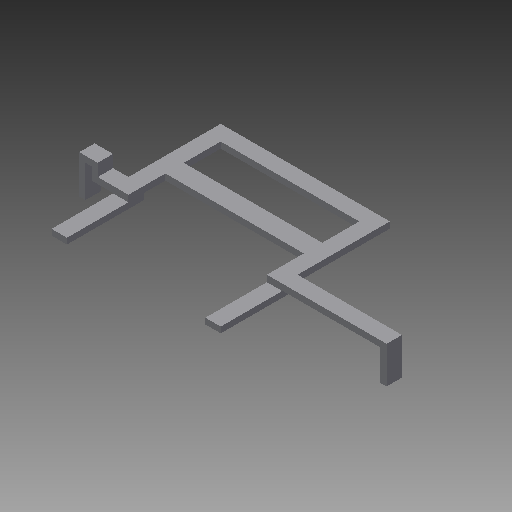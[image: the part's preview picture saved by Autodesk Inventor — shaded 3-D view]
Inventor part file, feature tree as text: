
AUTODESK INVENTOR PART (.ipt)
format: ipt  version: 2018.3 (Build 223284000, 284)  size: 192,512 bytes
history: native  units: mm
features: extrude x12, sketch x12
ambient origin geometry x8: Origin, YZ Plane, XZ Plane, XY Plane, X Axis, Y Axis, Z Axis, Center Point
bodies: Solid1 (feature_tree)
feature tree (24):
  extrude  "Extrusion1"  Depth=12.5mm
  extrude  "Extrusion2"  Depth=2.0mm
  extrude  "Extrusion3"  Depth=4.0mm
  extrude  "Extrusion4"  Depth=2.0mm
  extrude  "Extrusion5"  Depth=30.0mm TaperAngle=0.0deg
  extrude  "Extrusion6"  Depth=50.0mm TaperAngle=0.0deg
  extrude  "Extrusion7"  Depth=30.0mm TaperAngle=0.0deg
  extrude  "Extrusion8"  Depth=4.0mm TaperAngle=0.0deg
  extrude  "Extrusion9"  Depth=10.0mm TaperAngle=0.0deg
  extrude  "Extrusion10"  Depth=1.9mm
  extrude  "Extrusion11"  Depth=1.9mm
  extrude  "Extrusion12"  Depth=6.0mm
  sketch  "Sketch1"  dims[d0=2.0mm d1=12.5mm]
  sketch  "Sketch2"  dims[d2=4.0mm d3=2.0mm]
  sketch  "Sketch3"  dims[d4=2.0mm d5=4.0mm]
  sketch  "Sketch4"  dims[d6=5.0mm d7=0.0mm d8=2.0mm]
  sketch  "Sketch5"  dims[d9=10.0mm d10=0.0mm d11=30.0mm d12=0.0mm]
  sketch  "Sketch6"  dims[d13=5.0mm d14=50.0mm d15=0.0mm]
  sketch  "Sketch7"  dims[d16=5.0mm d17=30.0mm d18=0.0mm]
  sketch  "Sketch8"  dims[d19=29.93mm d20=0.0mm d21=4.0mm d22=0.0mm]
  sketch  "Sketch9"  dims[d23=2.0mm d24=10.0mm d25=0.0mm]
  sketch  "Sketch10"  dims[d26=2.0mm d27=0.0mm d28=1.9mm]
  sketch  "Sketch11"  dims[d29=20.0mm d30=0.0mm d31=1.9mm]
  sketch  "Sketch12"  dims[d32=20.0mm d33=0.0mm d34=6.0mm d35=12.0mm d36=10.0mm d37=0.0mm]
